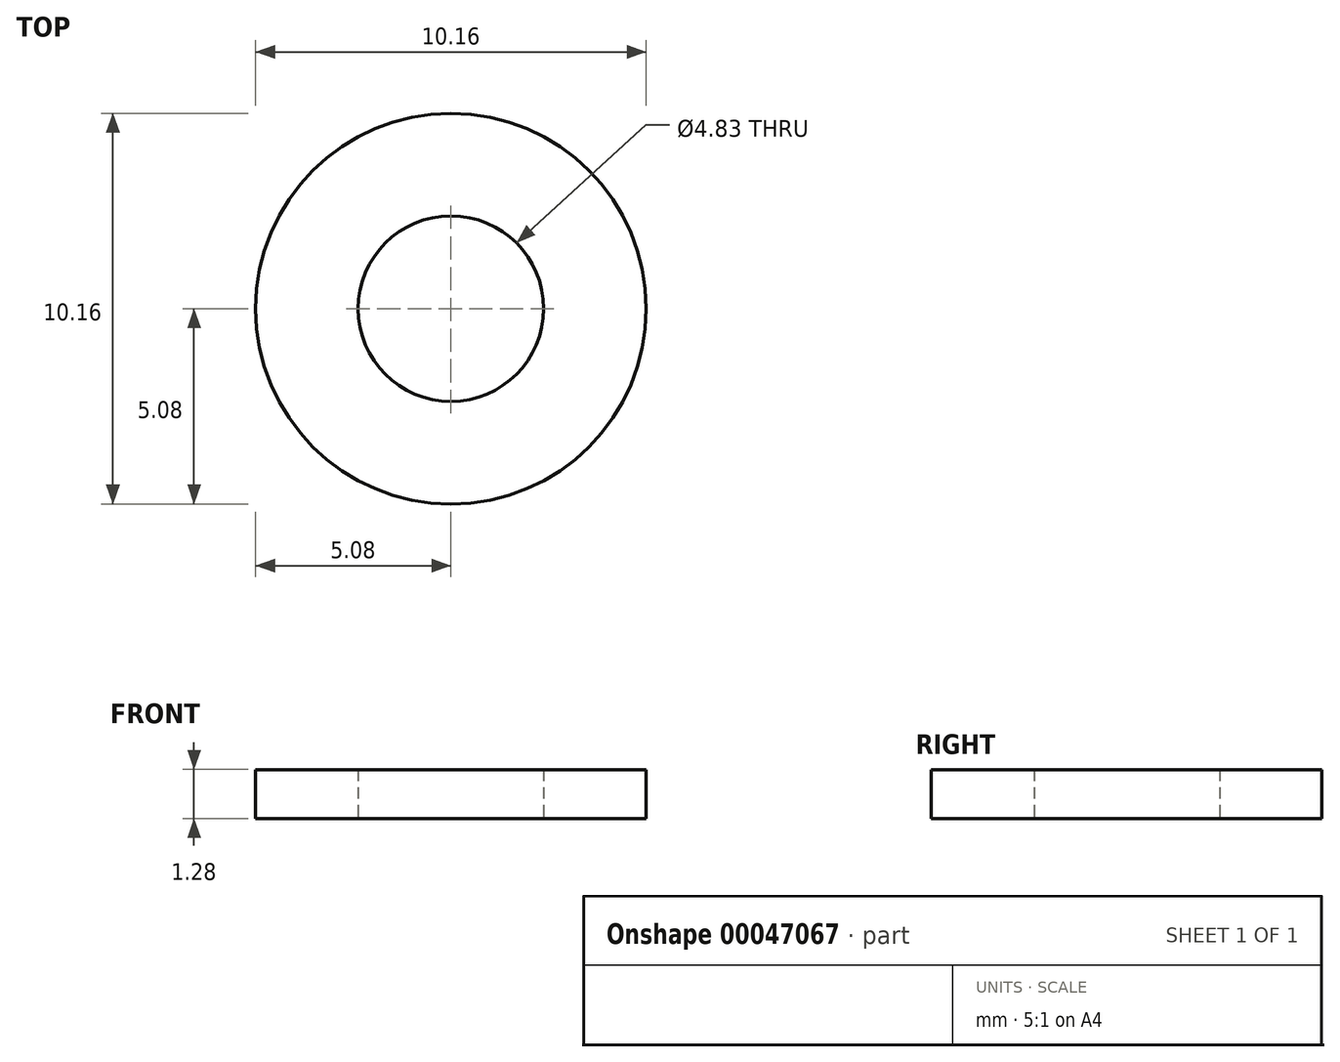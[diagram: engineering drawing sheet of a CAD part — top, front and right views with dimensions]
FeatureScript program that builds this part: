
annotation { "Feature Type Name" : "Feature", "Feature Type Description" : "" }
export const myFeature = defineFeature(function(context is Context, id is Id, definition is map)
    precondition{}
    {
        {
            var Q0;
            Q0=qCreatedBy(makeId("Top.planeOp"),FACE);
            var sketch = newSketch(context, id + "F0", { "sketchPlane" : qUnion([Q0])});
            skCircle(sketch, "E0", {"center": v(0, 0) * mm, "radius": 5.08 * mm});
            skCircle(sketch, "E1", {"center": v(0, 0) * mm, "radius": 2.41 * mm});
            skSolve(sketch);
        }
        {
            var Q0;
            Q0=makeQuery(id+"F0.imprint","IMPRINT",FACE,{"disambiguationData":[TD([[makeQuery(id+"F0.imprint","IMPRINT",EDGE,{"derivedFrom":sQuery(id+"F0.wireOp",EDGE,"E0")}),1.0]])]});
            extrude(context, id + "F1", {"entities" : qUnion([Q0]), "endBound" : BoundingType.SYMMETRIC, "depth" : 1.27 * mm});
        }
    });
